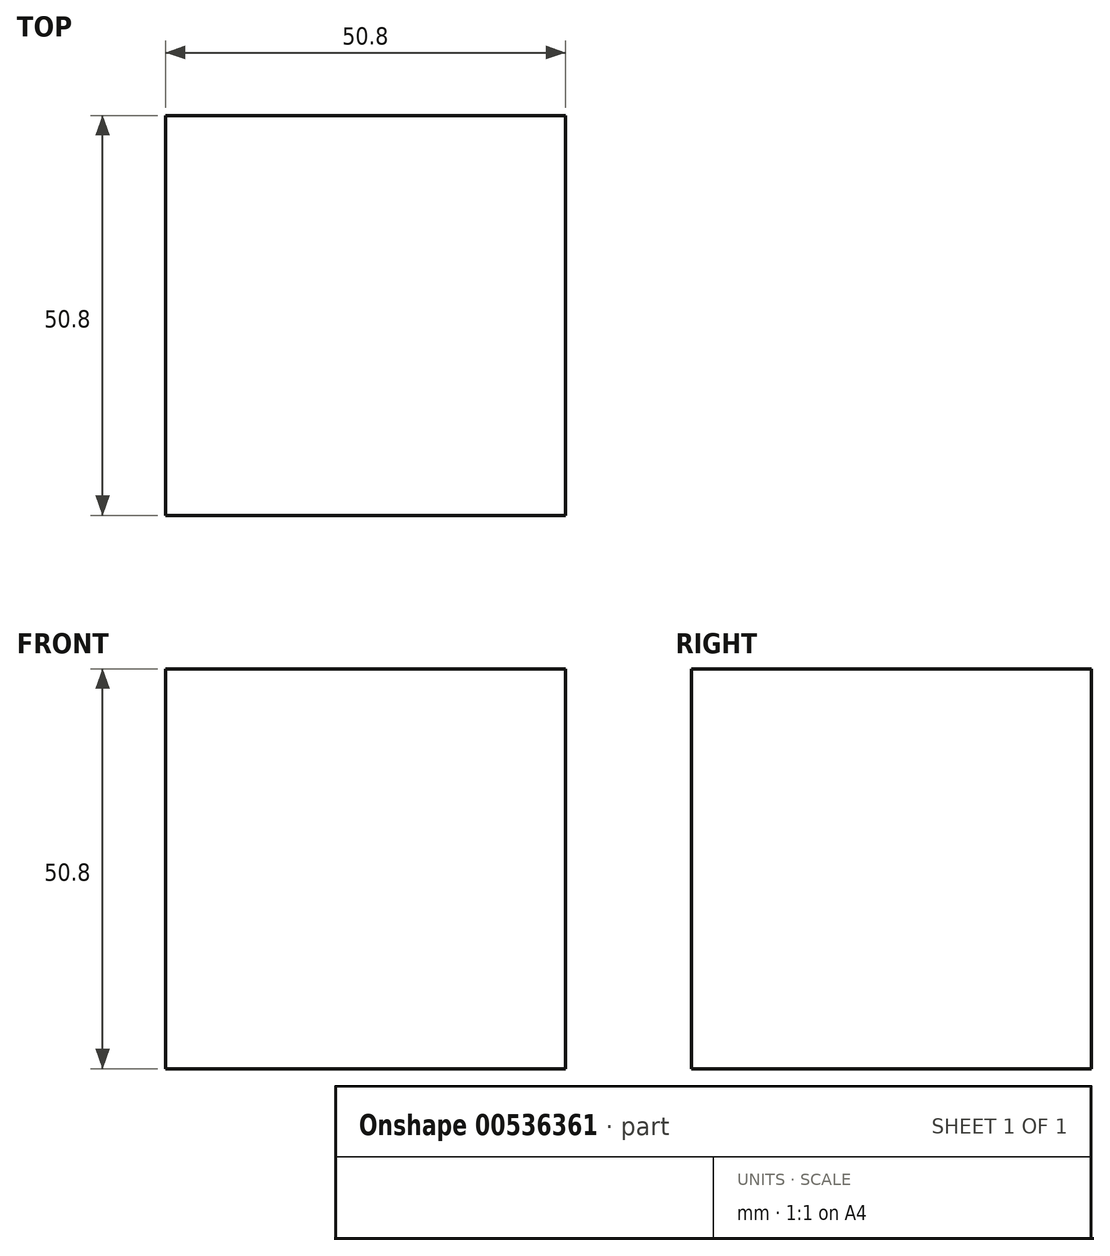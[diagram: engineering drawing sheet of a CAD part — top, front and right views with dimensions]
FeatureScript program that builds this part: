
annotation { "Feature Type Name" : "Feature", "Feature Type Description" : "" }
export const myFeature = defineFeature(function(context is Context, id is Id, definition is map)
    precondition{}
    {
        {
            var Q0;
            Q0=qCreatedBy(makeId("Front.planeOp"),FACE);
            var sketch = newSketch(context, id + "F0", { "sketchPlane" : qUnion([Q0])});
            skLineSegment(sketch, "E0.bottom", {"start": v(25.4, 25.4) * mm, "end": v(-25.4, 25.4) * mm});
            skLineSegment(sketch, "E0.top", {"start": v(25.4, -25.4) * mm, "end": v(-25.4, -25.4) * mm});
            skLineSegment(sketch, "E0.left", {"start": v(25.4, 25.4) * mm, "end": v(25.4, -25.4) * mm});
            skLineSegment(sketch, "E0.right", {"start": v(-25.4, 25.4) * mm, "end": v(-25.4, -25.4) * mm});
            skPoint(sketch, "E0.middle", {"position": v(0, 0) * mm});
            skSolve(sketch);
        }
        {
            var Q0;
            Q0=makeQuery(id+"F0.imprint","IMPRINT",FACE,{"disambiguationData":[TD([[makeQuery(id+"F0.imprint","IMPRINT",EDGE,{"derivedFrom":sQuery(id+"F0.wireOp",EDGE,"E0.bottom")}),1.0]])]});
            extrude(context, id + "F1", {"entities" : qUnion([Q0]), "endBound" : BoundingType.SYMMETRIC, "depth" : 50.8 * mm, "offsetDistance" : 25.4 * mm});
        }
    });
